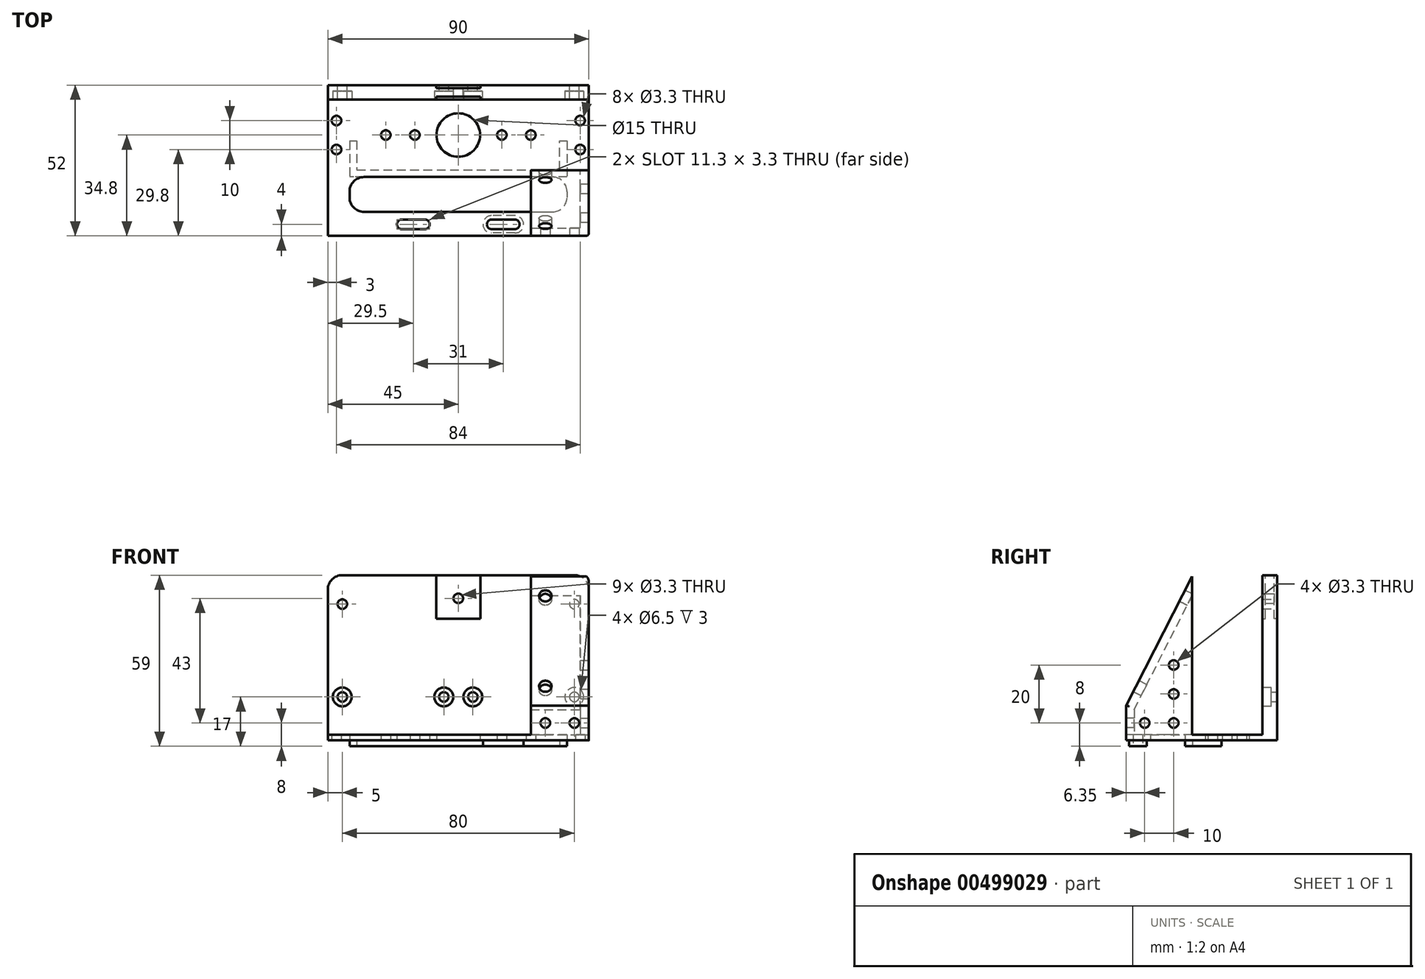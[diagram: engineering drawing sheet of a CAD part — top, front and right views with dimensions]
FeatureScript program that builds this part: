
annotation { "Feature Type Name" : "Feature", "Feature Type Description" : "" }
export const myFeature = defineFeature(function(context is Context, id is Id, definition is map)
    precondition{}
    {
        {
            var Q0;
            Q0=qCreatedBy(makeId("Top.planeOp"),FACE);
            var sketch = newSketch(context, id + "F0", { "sketchPlane" : qUnion([Q0])});
            skLineSegment(sketch, "E0.bottom", {"start": v(-45, 17.2) * mm, "end": v(45, 17.2) * mm});
            skLineSegment(sketch, "E0.top", {"start": v(-45, -34.8) * mm, "end": v(45, -34.8) * mm});
            skLineSegment(sketch, "E0.left", {"start": v(-45, 17.2) * mm, "end": v(-45, -34.8) * mm});
            skLineSegment(sketch, "E0.right", {"start": v(45, 17.2) * mm, "end": v(45, -34.8) * mm});
            skPoint(sketch, "E1", {"position": v(0, 17.2) * mm});
            skPoint(sketch, "E2", {"position": v(45, -8.8) * mm});
            skLineSegment(sketch, "E3.bottom", {"start": v(-35, 12) * mm, "end": v(35, 12) * mm, "construction": true});
            skLineSegment(sketch, "E3.top", {"start": v(-35, -12) * mm, "end": v(35, -12) * mm, "construction": true});
            skLineSegment(sketch, "E3.left", {"start": v(-35, 12) * mm, "end": v(-35, -12) * mm, "construction": true});
            skLineSegment(sketch, "E3.right", {"start": v(35, 12) * mm, "end": v(35, -12) * mm, "construction": true});
            skPoint(sketch, "E4", {"position": v(0, 12) * mm});
            skPoint(sketch, "E5", {"position": v(35, 0) * mm});
            skCircle(sketch, "E6", {"center": v(-15, 0) * mm, "radius": 1.65 * mm});
            skLineSegment(sketch, "E7", {"start": v(-35, -12) * mm, "end": v(35, -12) * mm});
            skLineSegment(sketch, "E8", {"start": v(35, -12) * mm, "end": v(35, -2) * mm});
            skLineSegment(sketch, "E9", {"start": v(35, -2) * mm, "end": v(37.5, -2) * mm});
            skLineSegment(sketch, "E10", {"start": v(37.5, -2) * mm, "end": v(37.5, -14.5) * mm});
            skLineSegment(sketch, "E11", {"start": v(37.5, -14.5) * mm, "end": v(-37.5, -14.5) * mm});
            skLineSegment(sketch, "E12", {"start": v(-37.5, -14.5) * mm, "end": v(-37.5, -2) * mm});
            skLineSegment(sketch, "E13", {"start": v(-37.5, -2) * mm, "end": v(-35, -2) * mm});
            skLineSegment(sketch, "E14", {"start": v(-35, -2) * mm, "end": v(-35, -12) * mm});
            skLineSegment(sketch, "E15", {"start": v(-35, -12) * mm, "end": v(-37.5, -12) * mm});
            skLineSegment(sketch, "E16", {"start": v(35, -12) * mm, "end": v(37.5, -12) * mm});
            skCircle(sketch, "E17", {"center": v(-19.5, -30.8) * mm, "radius": 1.65 * mm});
            skCircle(sketch, "E18", {"center": v(-11.5, -30.8) * mm, "radius": 1.65 * mm});
            skLineSegment(sketch, "E19.bottom", {"start": v(-19.5, -29.15) * mm, "end": v(-11.5, -29.15) * mm});
            skLineSegment(sketch, "E19.top", {"start": v(-19.5, -32.45) * mm, "end": v(-11.5, -32.45) * mm});
            skLineSegment(sketch, "E19.left", {"start": v(-19.5, -29.15) * mm, "end": v(-19.5, -32.45) * mm});
            skLineSegment(sketch, "E19.right", {"start": v(-11.5, -29.15) * mm, "end": v(-11.5, -32.45) * mm});
            skLineSegment(sketch, "E20", {"start": v(-19.5, -30.8) * mm, "end": v(-11.5, -30.8) * mm, "construction": true});
            skPoint(sketch, "E21", {"position": v(-15.5, -30.8) * mm});
            skCircle(sketch, "E22.MirrorC", {"center": v(19.5, -30.8) * mm, "radius": 1.65 * mm});
            skCircle(sketch, "E23.MirrorC", {"center": v(11.5, -30.8) * mm, "radius": 1.65 * mm});
            skLineSegment(sketch, "E24.MirrorCS", {"start": v(19.5, -29.15) * mm, "end": v(11.5, -29.15) * mm});
            skLineSegment(sketch, "E25.MirrorCS", {"start": v(19.5, -32.45) * mm, "end": v(11.5, -32.45) * mm});
            skPoint(sketch, "E26.MirrorP", {"position": v(15.5, -30.8) * mm});
            skLineSegment(sketch, "E27.bottom", {"start": v(-37.5, -14.5) * mm, "end": v(37.5, -14.5) * mm});
            skLineSegment(sketch, "E27.top", {"start": v(-37.5, -26.5) * mm, "end": v(37.5, -26.5) * mm});
            skLineSegment(sketch, "E27.left", {"start": v(-37.5, -14.5) * mm, "end": v(-37.5, -26.5) * mm});
            skLineSegment(sketch, "E27.right", {"start": v(37.5, -14.5) * mm, "end": v(37.5, -26.5) * mm});
            skCircle(sketch, "E28", {"center": v(-25, 0) * mm, "radius": 1.65 * mm});
            skCircle(sketch, "E29.MirrorC", {"center": v(15, 0) * mm, "radius": 1.65 * mm});
            skCircle(sketch, "E30.MirrorC", {"center": v(25, 0) * mm, "radius": 1.65 * mm});
            skCircle(sketch, "E31", {"center": v(0, 0) * mm, "radius": 7.5 * mm});
            skCircle(sketch, "E32", {"center": v(-42, 5) * mm, "radius": 1.65 * mm});
            skCircle(sketch, "E33", {"center": v(-42, -5) * mm, "radius": 1.65 * mm});
            skLineSegment(sketch, "E34", {"start": v(-42, 5) * mm, "end": v(-42, -5) * mm, "construction": true});
            skPoint(sketch, "E35", {"position": v(-42, 0) * mm});
            skCircle(sketch, "E36.MirrorC", {"center": v(42, 5) * mm, "radius": 1.65 * mm});
            skCircle(sketch, "E37.MirrorC", {"center": v(42, -5) * mm, "radius": 1.65 * mm});
            skSolve(sketch);
        }
        {
            var Q0;
            Q0=makeQuery(id+"F0.imprint","IMPRINT",FACE,{"disambiguationData":[TD([[makeQuery(id+"F0.imprint","IMPRINT",EDGE,{"derivedFrom":sQuery(id+"F0.wireOp",EDGE,"E0.bottom")}),-1.0]])]});
            var Q1;
            Q1=makeQuery(id+"F0.imprint","IMPRINT",FACE,{"disambiguationData":[TD([[makeQuery(id+"F0.imprint","IMPRINT",EDGE,{"derivedFrom":sQuery(id+"F0.wireOp",EDGE,"E7")}),-1.0]])]});
            var Q2;
            {var subQ0=sQuery(id+"F0.wireOp",EDGE,"E13");Q2=makeQuery(id+"F0.imprint","IMPRINT",FACE,{"disambiguationData":[TD([[makeQuery(id+"F0.imprint","IMPRINT",EDGE,{"derivedFrom":subQ0}),-1.0]])]});}
            var Q3;
            Q3=makeQuery(id+"F0.imprint","IMPRINT",FACE,{"disambiguationData":[TD([[makeQuery(id+"F0.imprint","IMPRINT",EDGE,{"derivedFrom":sQuery(id+"F0.wireOp",EDGE,"E8")}),-1.0]])]});
            extrude(context, id + "F1", {"entities" : qUnion([Q0, Q1, Q2, Q3]), "depth" : 4 * mm});
        }
        {
            var Q0;
            {var subQ0=sQuery(id+"F0.wireOp",EDGE,"E13");Q0=makeQuery(id+"F0.imprint","IMPRINT",FACE,{"disambiguationData":[TD([[makeQuery(id+"F0.imprint","IMPRINT",EDGE,{"derivedFrom":subQ0}),-1.0]])]});}
            var Q1;
            Q1=makeQuery(id+"F0.imprint","IMPRINT",FACE,{"disambiguationData":[TD([[makeQuery(id+"F0.imprint","IMPRINT",EDGE,{"derivedFrom":sQuery(id+"F0.wireOp",EDGE,"E8")}),-1.0]])]});
            extrude(context, id + "F2", {"entities" : qUnion([Q0, Q1]), "operationType" : NewBodyOperationType.ADD, "offsetDistance" : 25 * mm, "depth" : 3 * mm});
        }
        {
            var Q0;
            Q0=makeQuery(id+"F1.opExtrude","CAP_FACE",FACE,{"disambiguationData":[OSD([sQuery(id+"F0.wireOp",EDGE,"E0.bottom"),sQuery(id+"F0.wireOp",EDGE,"E0.top"),sQuery(id+"F0.wireOp",EDGE,"E0.left"),sQuery(id+"F0.wireOp",EDGE,"E0.right"),sQuery(id+"F0.wireOp",EDGE,"E6")])],"isStart":false});
            var sketch = newSketch(context, id + "F3", { "sketchPlane" : qUnion([Q0])});
            skLineSegment(sketch, "E38.bottom", {"start": v(-45, 17.2) * mm, "end": v(45, 17.2) * mm});
            skLineSegment(sketch, "E38.top", {"start": v(-45, 12.2) * mm, "end": v(45, 12.2) * mm});
            skLineSegment(sketch, "E38.left", {"start": v(-45, 17.2) * mm, "end": v(-45, 12.2) * mm});
            skLineSegment(sketch, "E38.right", {"start": v(45, 17.2) * mm, "end": v(45, 12.2) * mm});
            skSolve(sketch);
        }
        {
            var Q0;
            Q0=makeQuery(id+"F3.imprint","IMPRINT",FACE,{"disambiguationData":[TD([[makeQuery(id+"F3.imprint","IMPRINT",EDGE,{"derivedFrom":sQuery(id+"F3.wireOp",EDGE,"E38.bottom")}),-1.0]])]});
            extrude(context, id + "F4", {"entities" : qUnion([Q0]), "operationType" : NewBodyOperationType.ADD, "depth" : 55 * mm});
        }
        {
            var Q0;
            Q0=makeQuery(id+"F4.opExtrude","CAP_FACE",FACE,{"disambiguationData":[OSD([sQuery(id+"F3.wireOp",EDGE,"E38.bottom"),sQuery(id+"F3.wireOp",EDGE,"E38.top"),sQuery(id+"F3.wireOp",EDGE,"E38.left"),sQuery(id+"F3.wireOp",EDGE,"E38.right")])],"isStart":false});
            var sketch = newSketch(context, id + "F5", { "sketchPlane" : qUnion([Q0])});
            skLineSegment(sketch, "E39.bottom", {"start": v(-7.65, 17.2) * mm, "end": v(7.65, 17.2) * mm});
            skLineSegment(sketch, "E39.top", {"start": v(-7.65, 16.2) * mm, "end": v(7.65, 16.2) * mm});
            skLineSegment(sketch, "E39.left", {"start": v(-7.65, 17.2) * mm, "end": v(-7.65, 16.2) * mm});
            skLineSegment(sketch, "E39.right", {"start": v(7.65, 17.2) * mm, "end": v(7.65, 16.2) * mm});
            skLineSegment(sketch, "E40.bottom", {"start": v(-7.65, 12.2) * mm, "end": v(7.65, 12.2) * mm});
            skLineSegment(sketch, "E40.top", {"start": v(-7.65, 13.2) * mm, "end": v(7.65, 13.2) * mm});
            skLineSegment(sketch, "E40.left", {"start": v(-7.65, 12.2) * mm, "end": v(-7.65, 13.2) * mm});
            skLineSegment(sketch, "E40.right", {"start": v(7.65, 12.2) * mm, "end": v(7.65, 13.2) * mm});
            skPoint(sketch, "E41", {"position": v(0, 17.2) * mm});
            skSolve(sketch);
        }
        {
            var Q0;
            Q0=makeQuery(id+"F5.imprint","IMPRINT",FACE,{"disambiguationData":[TD([[makeQuery(id+"F5.imprint","IMPRINT",EDGE,{"derivedFrom":sQuery(id+"F5.wireOp",EDGE,"E39.bottom")}),-1.0]])]});
            var Q1;
            Q1=makeQuery(id+"F5.imprint","IMPRINT",FACE,{"disambiguationData":[TD([[makeQuery(id+"F5.imprint","IMPRINT",EDGE,{"derivedFrom":sQuery(id+"F5.wireOp",EDGE,"E40.bottom")}),1.0]])]});
            extrude(context, id + "F6", {"entities" : qUnion([Q0, Q1]), "operationType" : NewBodyOperationType.REMOVE, "oppositeDirection" : true, "depth" : 15 * mm});
        }
        {
            var Q0;
            Q0=makeQuery(id+"F6.boolean.opBoolean","COPY",FACE,{"derivedFrom":makeQuery(id+"F6.opExtrude","SWEPT_FACE",FACE,{"disambiguationData":[OSD([sQuery(id+"F5.wireOp",EDGE,"E39.top")])]})});
            var sketch = newSketch(context, id + "F7", { "sketchPlane" : qUnion([Q0])});
            skCircle(sketch, "E42", {"center": v(0, 51) * mm, "radius": 1.65 * mm});
            skSolve(sketch);
        }
        {
            var Q0;
            Q0=makeQuery(id+"F7.imprint","IMPRINT",FACE,{"disambiguationData":[TD([[makeQuery(id+"F7.imprint","IMPRINT",EDGE,{"derivedFrom":sQuery(id+"F7.wireOp",EDGE,"E42")}),1.0]])]});
            extrude(context, id + "F8", {"entities" : qUnion([Q0]), "operationType" : NewBodyOperationType.REMOVE, "endBound" : BoundingType.UP_TO_NEXT, "oppositeDirection" : true, "depth" : 25 * mm});
        }
        {
            var Q0;
            Q0=makeQuery(id+"F4.boolean.opBoolean","MERGE",FACE,{"derivedFrom":[makeQuery(id+"F1.opExtrude","SWEPT_FACE",FACE,{"disambiguationData":[OSD([sQuery(id+"F0.wireOp",EDGE,"E0.bottom")])]}),makeQuery(id+"F4.opExtrude","SWEPT_FACE",FACE,{"disambiguationData":[OSD([sQuery(id+"F3.wireOp",EDGE,"E38.bottom")])]})]});
            var sketch = newSketch(context, id + "F9", { "sketchPlane" : qUnion([Q0])});
            skLineSegment(sketch, "E43", {"start": v(-45, 17) * mm, "end": v(45, 17) * mm, "construction": true});
            skCircle(sketch, "E44", {"center": v(-40, 17) * mm, "radius": 1.65 * mm});
            skCircle(sketch, "E45", {"center": v(-5, 17) * mm, "radius": 1.65 * mm});
            skCircle(sketch, "E46.MirrorC", {"center": v(40, 17) * mm, "radius": 1.65 * mm});
            skCircle(sketch, "E47.MirrorC", {"center": v(5, 17) * mm, "radius": 1.65 * mm});
            skCircle(sketch, "E48", {"center": v(-40, 49) * mm, "radius": 1.65 * mm});
            skCircle(sketch, "E49.MirrorC", {"center": v(40, 49) * mm, "radius": 1.65 * mm});
            skSolve(sketch);
        }
        {
            var Q0;
            Q0 = qSketchRegion(id + "F9", true);
            extrude(context, id + "F10", {"entities" : qUnion([Q0]), "operationType" : NewBodyOperationType.REMOVE, "endBound" : BoundingType.UP_TO_NEXT, "oppositeDirection" : true, "depth" : 25 * mm});
        }
        {
            var Q0;
            Q0=makeQuery(id+"F4.opExtrude","SWEPT_FACE",FACE,{"disambiguationData":[OSD([sQuery(id+"F3.wireOp",EDGE,"E38.top")])]});
            var sketch = newSketch(context, id + "F11", { "sketchPlane" : qUnion([Q0])});
            skCircle(sketch, "E50", {"center": v(5, 17) * mm, "radius": 3.25 * mm});
            skCircle(sketch, "E51", {"center": v(40, 17) * mm, "radius": 3.25 * mm});
            skCircle(sketch, "E52.MirrorC", {"center": v(-5, 17) * mm, "radius": 3.25 * mm});
            skCircle(sketch, "E53.MirrorC", {"center": v(-40, 17) * mm, "radius": 3.25 * mm});
            skSolve(sketch);
        }
        {
            var Q0;
            Q0 = qSketchRegion(id + "F11", true);
            extrude(context, id + "F12", {"entities" : qUnion([Q0]), "operationType" : NewBodyOperationType.REMOVE, "oppositeDirection" : true, "depth" : 3 * mm});
        }
        {
            var Q0;
            Q0=makeQuery(id+"F0.imprint","IMPRINT",FACE,{"disambiguationData":[TD([[makeQuery(id+"F0.imprint","IMPRINT",EDGE,{"derivedFrom":sQuery(id+"F0.wireOp",EDGE,"E0.bottom")}),-1.0]])]});
            var sketch = newSketch(context, id + "F13", { "sketchPlane" : qUnion([Q0])});
            skPoint(sketch, "E54.0", {"position": v(-15.5, -30.8) * mm});
            skLineSegment(sketch, "E55.bottom", {"start": v(-19.5, -33.8) * mm, "end": v(-11.5, -33.8) * mm});
            skLineSegment(sketch, "E55.top", {"start": v(-19.5, -27.8) * mm, "end": v(-11.5, -27.8) * mm});
            skLineSegment(sketch, "E55.left", {"start": v(-22.5, -30.8) * mm, "end": v(-22.5, -30.8) * mm});
            skLineSegment(sketch, "E55.right", {"start": v(-8.5, -30.8) * mm, "end": v(-8.5, -30.8) * mm});
            skPoint(sketch, "E56", {"position": v(-15.5, -33.8) * mm});
            skPoint(sketch, "E57", {"position": v(-22.5, -30.8) * mm});
            skPoint(sketch, "E58.visualSharp", {"position": v(-22.5, -33.8) * mm});
            skArc(sketch, "E58.filletArc", {"start": v(-22.5, -30.8) * mm, "mid": v(-21.62, -32.92) * mm, "end": v(-19.5, -33.8) * mm});
            skPoint(sketch, "E59.visualSharp", {"position": v(-22.5, -27.8) * mm});
            skArc(sketch, "E59.filletArc", {"start": v(-19.5, -27.8) * mm, "mid": v(-21.62, -28.68) * mm, "end": v(-22.5, -30.8) * mm});
            skPoint(sketch, "E60.visualSharp", {"position": v(-8.5, -27.8) * mm});
            skArc(sketch, "E60.filletArc", {"start": v(-8.5, -30.8) * mm, "mid": v(-9.38, -28.68) * mm, "end": v(-11.5, -27.8) * mm});
            skPoint(sketch, "E61.visualSharp", {"position": v(-8.5, -33.8) * mm});
            skArc(sketch, "E61.filletArc", {"start": v(-11.5, -33.8) * mm, "mid": v(-9.38, -32.92) * mm, "end": v(-8.5, -30.8) * mm});
            skArc(sketch, "E62.MirrorCS", {"start": v(11.5, -33.8) * mm, "mid": v(9.38, -32.92) * mm, "end": v(8.5, -30.8) * mm});
            skLineSegment(sketch, "E63.MirrorCS", {"start": v(19.5, -33.8) * mm, "end": v(11.5, -33.8) * mm});
            skArc(sketch, "E64.MirrorCS", {"start": v(22.5, -30.8) * mm, "mid": v(21.62, -32.92) * mm, "end": v(19.5, -33.8) * mm});
            skArc(sketch, "E65.MirrorCS", {"start": v(19.5, -27.8) * mm, "mid": v(21.62, -28.68) * mm, "end": v(22.5, -30.8) * mm});
            skLineSegment(sketch, "E66.MirrorCS", {"start": v(19.5, -27.8) * mm, "end": v(11.5, -27.8) * mm});
            skArc(sketch, "E67.MirrorCS", {"start": v(8.5, -30.8) * mm, "mid": v(9.38, -28.68) * mm, "end": v(11.5, -27.8) * mm});
            skSolve(sketch);
        }
        {
            var Q0;
            Q0=makeQuery(id+"F13.imprint","IMPRINT",FACE,{"disambiguationData":[TD([[makeQuery(id+"F13.imprint","IMPRINT",EDGE,{"derivedFrom":sQuery(id+"F13.wireOp",EDGE,"E55.bottom")}),1.0]])]});
            var Q1;
            Q1=makeQuery(id+"F13.imprint","IMPRINT",FACE,{"disambiguationData":[TD([[makeQuery(id+"F13.imprint","IMPRINT",EDGE,{"derivedFrom":sQuery(id+"F13.wireOp",EDGE,"E62.MirrorCS")}),-1.0]])]});
            extrude(context, id + "F14", {"entities" : qUnion([Q0, Q1]), "operationType" : NewBodyOperationType.REMOVE, "depth" : 2 * mm});
        }
        {
            var Q0;
            Q0=makeQuery(id+"F4.boolean.opBoolean","MERGE",FACE,{"derivedFrom":[makeQuery(id+"F1.opExtrude","SWEPT_FACE",FACE,{"disambiguationData":[OSD([sQuery(id+"F0.wireOp",EDGE,"E0.right")])]}),makeQuery(id+"F4.opExtrude","SWEPT_FACE",FACE,{"disambiguationData":[OSD([sQuery(id+"F3.wireOp",EDGE,"E38.right")])]})]});
            var sketch = newSketch(context, id + "F15", { "sketchPlane" : qUnion([Q0])});
            skLineSegment(sketch, "E68", {"start": v(-34.8, 4) * mm, "end": v(-34.8, 14) * mm});
            skLineSegment(sketch, "E69", {"start": v(-34.8, 14) * mm, "end": v(-12.1, 58.55) * mm});
            skLineSegment(sketch, "E70", {"start": v(-12.1, 58.55) * mm, "end": v(-12.1, 4) * mm});
            skLineSegment(sketch, "E71", {"start": v(-12.1, 4) * mm, "end": v(-34.8, 4) * mm});
            skLineSegment(sketch, "E72", {"start": v(-34.8, 14) * mm, "end": v(-32.13, 12.64) * mm});
            skLineSegment(sketch, "E73", {"start": v(-32.13, 12.64) * mm, "end": v(-12.1, 51.94) * mm});
            skLineSegment(sketch, "E74", {"start": v(-12.1, 58.55) * mm, "end": v(-12.1, 51.94) * mm});
            skLineSegment(sketch, "E75", {"start": v(-32.13, 12.64) * mm, "end": v(-32.13, 4) * mm});
            skLineSegment(sketch, "E76", {"start": v(-32.13, 4) * mm, "end": v(-34.8, 4) * mm});
            skSolve(sketch);
        }
        {
            var Q0;
            Q0=makeQuery(id+"F15.imprint","IMPRINT",FACE,{"disambiguationData":[TD([[makeQuery(id+"F15.imprint","IMPRINT",EDGE,{"derivedFrom":sQuery(id+"F15.wireOp",EDGE,"E68")}),-1.0]])]});
            var Q1;
            {var subQ0=sQuery(id+"F15.wireOp",EDGE,"E72");Q1=makeQuery(id+"F15.imprint","IMPRINT",FACE,{"disambiguationData":[TD([[makeQuery(id+"F15.imprint","IMPRINT",EDGE,{"derivedFrom":subQ0}),1.0]])]});}
            var Q2;
            Q2=makeQuery(id+"F15.imprint","IMPRINT",FACE,{"disambiguationData":[TD([[makeQuery(id+"F15.imprint","IMPRINT",EDGE,{"derivedFrom":sQuery(id+"F15.wireOp",EDGE,"E74")}),-1.0]])]});
            var Q3;
            Q3=makeQuery(id+"F15.imprint","IMPRINT",FACE,{"disambiguationData":[TD([[makeQuery(id+"F15.imprint","IMPRINT",EDGE,{"derivedFrom":sQuery(id+"F15.wireOp",EDGE,"E73")}),1.0]])]});
            var Q4;
            Q4=makeQuery(id+"F15.imprint","IMPRINT",FACE,{"disambiguationData":[TD([[makeQuery(id+"F15.imprint","IMPRINT",EDGE,{"derivedFrom":sQuery(id+"F15.wireOp",EDGE,"E70")}),-1.0]])]});
            extrude(context, id + "F16", {"entities" : qUnion([Q0, Q1, Q2, Q3, Q4]), "operationType" : NewBodyOperationType.ADD, "oppositeDirection" : true, "depth" : 3 * mm});
        }
        {
            var Q0;
            Q0=makeQuery(id+"F15.imprint","IMPRINT",FACE,{"disambiguationData":[TD([[makeQuery(id+"F15.imprint","IMPRINT",EDGE,{"derivedFrom":sQuery(id+"F15.wireOp",EDGE,"E68")}),-1.0]])]});
            var Q1;
            Q1=makeQuery(id+"F15.imprint","IMPRINT",FACE,{"disambiguationData":[TD([[makeQuery(id+"F15.imprint","IMPRINT",EDGE,{"derivedFrom":sQuery(id+"F15.wireOp",EDGE,"E73")}),1.0]])]});
            var Q2;
            Q2=makeQuery(id+"F15.imprint","IMPRINT",FACE,{"disambiguationData":[TD([[makeQuery(id+"F15.imprint","IMPRINT",EDGE,{"derivedFrom":sQuery(id+"F15.wireOp",EDGE,"E74")}),-1.0]])]});
            extrude(context, id + "F17", {"entities" : qUnion([Q0, Q1, Q2]), "operationType" : NewBodyOperationType.ADD, "oppositeDirection" : true, "depth" : 20 * mm});
        }
        {
            var Q0;
            {var subQ0=sQuery(id+"F15.wireOp",EDGE,"1dctdDmi-W59R-1fRP-TE5Q-M4lD137gEtmT");var subQ1=sQuery(id+"F15.wireOp",EDGE,"E69");Q0=makeQuery(id+"F17.boolean.opBoolean","MERGE",FACE,{"derivedFrom":[makeQuery(id+"F16.opExtrude","SWEPT_FACE",FACE,{"disambiguationData":[OSD([subQ1,subQ0])]}),makeQuery(id+"F17.opExtrude","SWEPT_FACE",FACE,{"disambiguationData":[OSD([subQ1])]}),makeQuery(id+"F17.opExtrude","SWEPT_FACE",FACE,{"disambiguationData":[OSD([subQ0])]})]});}
            var sketch = newSketch(context, id + "F18", { "sketchPlane" : qUnion([Q0])});
            skCircle(sketch, "E77", {"center": v(30, 39.18) * mm, "radius": 2.15 * mm});
            skCircle(sketch, "E78", {"center": v(30, 4.18) * mm, "radius": 2.15 * mm});
            skLineSegment(sketch, "E79", {"start": v(30, 39.18) * mm, "end": v(30, 4.18) * mm, "construction": true});
            skPoint(sketch, "E80", {"position": v(30, 21.68) * mm});
            skPoint(sketch, "E81", {"position": v(45, 21.68) * mm});
            skSolve(sketch);
        }
        {
            var Q0;
            Q0=makeQuery(id+"F18.imprint","IMPRINT",FACE,{"disambiguationData":[TD([[makeQuery(id+"F18.imprint","IMPRINT",EDGE,{"derivedFrom":sQuery(id+"F18.wireOp",EDGE,"E78")}),1.0]])]});
            var Q1;
            Q1=makeQuery(id+"F18.imprint","IMPRINT",FACE,{"disambiguationData":[TD([[makeQuery(id+"F18.imprint","IMPRINT",EDGE,{"derivedFrom":sQuery(id+"F18.wireOp",EDGE,"E77")}),1.0]])]});
            extrude(context, id + "F19", {"entities" : qUnion([Q0, Q1]), "operationType" : NewBodyOperationType.REMOVE, "endBound" : BoundingType.UP_TO_NEXT, "oppositeDirection" : true, "depth" : 25 * mm});
        }
        {
            var Q0;
            {var subQ0=sQuery(id+"F15.wireOp",EDGE,"E68");Q0=makeQuery(id+"FYoWc9Rnscle1AE_1.1.F17.boolean.opBoolean","MERGE",FACE,{"derivedFrom":[makeQuery(id+"FYoWc9Rnscle1AE_1.1.F16.boolean.opBoolean","MERGE",FACE,{"derivedFrom":[makeQuery(id+"F17.boolean.opBoolean","MERGE",FACE,{"derivedFrom":[makeQuery(id+"F16.boolean.opBoolean","MERGE",FACE,{"derivedFrom":[makeQuery(id+"F1.opExtrude","SWEPT_FACE",FACE,{"disambiguationData":[OSD([sQuery(id+"F0.wireOp",EDGE,"E0.top")])]}),makeQuery(id+"F16.opExtrude","SWEPT_FACE",FACE,{"disambiguationData":[OSD([subQ0])]})]}),makeQuery(id+"F17.opExtrude","SWEPT_FACE",FACE,{"disambiguationData":[OSD([subQ0])]})]}),makeQuery(id+"FYoWc9Rnscle1AE_1.1.F16.opExtrude","SWEPT_FACE",FACE,{"disambiguationData":[OSD([subQ0])]})]}),makeQuery(id+"FYoWc9Rnscle1AE_1.1.F17.opExtrude","SWEPT_FACE",FACE,{"disambiguationData":[OSD([subQ0])]})]});}
            var sketch = newSketch(context, id + "F20", { "sketchPlane" : qUnion([Q0])});
            skCircle(sketch, "E82", {"center": v(40, 8) * mm, "radius": 1.65 * mm});
            skCircle(sketch, "E83", {"center": v(30, 8) * mm, "radius": 1.65 * mm});
            skLineSegment(sketch, "E84", {"start": v(30, 8) * mm, "end": v(40, 8) * mm, "construction": true});
            skPoint(sketch, "E85", {"position": v(35, 8) * mm});
            skPoint(sketch, "E86", {"position": v(35, 14) * mm});
            skSolve(sketch);
        }
        {
            var Q0;
            Q0 = qSketchRegion(id + "F20", true);
            extrude(context, id + "F21", {"entities" : qUnion([Q0]), "operationType" : NewBodyOperationType.REMOVE, "endBound" : BoundingType.UP_TO_NEXT, "oppositeDirection" : true, "depth" : 25 * mm});
        }
        {
            var Q0;
            Q0=makeQuery(id+"F16.boolean.opBoolean","MERGE",FACE,{"derivedFrom":[makeQuery(id+"F4.boolean.opBoolean","MERGE",FACE,{"derivedFrom":[makeQuery(id+"F1.opExtrude","SWEPT_FACE",FACE,{"disambiguationData":[OSD([sQuery(id+"F0.wireOp",EDGE,"E0.right")])]}),makeQuery(id+"F4.opExtrude","SWEPT_FACE",FACE,{"disambiguationData":[OSD([sQuery(id+"F3.wireOp",EDGE,"E38.right")])]})]}),makeQuery(id+"F16.opExtrude","CAP_FACE",FACE,{"disambiguationData":[OSD([sQuery(id+"F15.wireOp",EDGE,"E68"),sQuery(id+"F15.wireOp",EDGE,"E69"),sQuery(id+"F15.wireOp",EDGE,"E70"),sQuery(id+"F15.wireOp",EDGE,"E71"),sQuery(id+"F15.wireOp",EDGE,"E74"),sQuery(id+"F15.wireOp",EDGE,"1dctdDmi-W59R-1fRP-TE5Q-M4lD137gEtmT"),sQuery(id+"F15.wireOp",EDGE,"E76")])],"isStart":true})]});
            var sketch = newSketch(context, id + "F22", { "sketchPlane" : qUnion([Q0])});
            skCircle(sketch, "E87", {"center": v(-28.45, 8) * mm, "radius": 1.65 * mm});
            skCircle(sketch, "E88", {"center": v(-18.45, 8) * mm, "radius": 1.65 * mm});
            skLineSegment(sketch, "E89", {"start": v(-28.45, 8) * mm, "end": v(-18.45, 8) * mm, "construction": true});
            skPoint(sketch, "E90", {"position": v(-23.45, 8) * mm});
            skLineSegment(sketch, "E91", {"start": v(-18.45, 8) * mm, "end": v(-12.1, 8) * mm, "construction": true});
            skLineSegment(sketch, "E92", {"start": v(-28.45, 8) * mm, "end": v(-34.8, 8) * mm, "construction": true});
            skCircle(sketch, "E93", {"center": v(-18.45, 18) * mm, "radius": 1.65 * mm});
            skCircle(sketch, "E94", {"center": v(-18.45, 28) * mm, "radius": 1.65 * mm});
            skSolve(sketch);
        }
        {
            var Q0;
            Q0 = qSketchRegion(id + "F22", true);
            extrude(context, id + "F23", {"entities" : qUnion([Q0]), "operationType" : NewBodyOperationType.REMOVE, "endBound" : BoundingType.UP_TO_NEXT, "oppositeDirection" : true, "depth" : 25 * mm});
        }
        {
            var Q0;
            {var subQ0=sQuery(id+"F15.wireOp",EDGE,"1dctdDmi-W59R-1fRP-TE5Q-M4lD137gEtmT");var subQ1=sQuery(id+"F15.wireOp",EDGE,"E74");Q0=makeQuery(id+"F17.boolean.opBoolean","MERGE",EDGE,{"derivedFrom":[makeQuery(id+"F16.opExtrude","SWEPT_EDGE",EDGE,{"disambiguationData":[OSD([subQ1,subQ0])]}),makeQuery(id+"F17.opExtrude","SWEPT_EDGE",EDGE,{"disambiguationData":[OSD([subQ1,subQ0])]})]});}
            var Q1;
            Q1=makeQuery(id+"F16.boolean.opBoolean","MERGE",EDGE,{"derivedFrom":[makeQuery(id+"F1.opExtrude","SWEPT_EDGE",EDGE,{"disambiguationData":[OSD([sQuery(id+"F0.wireOp",EDGE,"E0.top"),sQuery(id+"F0.wireOp",EDGE,"E0.right")])]}),makeQuery(id+"F16.opExtrude","CAP_EDGE",EDGE,{"disambiguationData":[OSD([sQuery(id+"F15.wireOp",EDGE,"E68")])],"isStart":true})]});
            var Q2;
            Q2=makeQuery(id+"F16.opExtrude","CAP_EDGE",EDGE,{"disambiguationData":[OSD([sQuery(id+"F15.wireOp",EDGE,"E69"),sQuery(id+"F15.wireOp",EDGE,"1dctdDmi-W59R-1fRP-TE5Q-M4lD137gEtmT")])],"isStart":true});
            fillet(context, id + "F24", {"entities" : qUnion([Q0, Q1, Q2]), "radius" : 1 * mm, "tangentPropagation" : true, "allowEdgeOverflow" : false});
        }
        {
            var Q0;
            Q0=makeQuery(id+"F4.opExtrude","CAP_EDGE",EDGE,{"disambiguationData":[OSD([sQuery(id+"F3.wireOp",EDGE,"E38.right")])],"isStart":false});
            var Q1;
            Q1=makeQuery(id+"F4.opExtrude","CAP_EDGE",EDGE,{"disambiguationData":[OSD([sQuery(id+"F3.wireOp",EDGE,"E38.left")])],"isStart":false});
            var Q2;
            Q2=makeQuery(id+"FHVHkK3Abyfqzx4_1.opExtrude","CAP_EDGE",EDGE,{"disambiguationData":[OSD([sQuery(id+"F0.wireOp",EDGE,"E10")])],"isStart":false});
            var Q3;
            Q3=makeQuery(id+"FHVHkK3Abyfqzx4_1.opExtrude","CAP_EDGE",EDGE,{"disambiguationData":[OSD([sQuery(id+"F0.wireOp",EDGE,"E12")])],"isStart":false});
            var Q4;
            Q4=makeQuery(id+"F1.opExtrude","SWEPT_EDGE",EDGE,{"disambiguationData":[OSD([sQuery(id+"F0.wireOp",EDGE,"E27.top"),sQuery(id+"F0.wireOp",EDGE,"E27.right")])]});
            var Q5;
            Q5=makeQuery(id+"F1.opExtrude","SWEPT_EDGE",EDGE,{"disambiguationData":[OSD([sQuery(id+"F0.wireOp",EDGE,"E10"),sQuery(id+"F0.wireOp",EDGE,"E27.bottom"),sQuery(id+"F0.wireOp",EDGE,"E27.right")])]});
            var Q6;
            Q6=makeQuery(id+"F1.opExtrude","SWEPT_EDGE",EDGE,{"disambiguationData":[OSD([sQuery(id+"F0.wireOp",EDGE,"E12"),sQuery(id+"F0.wireOp",EDGE,"E27.bottom"),sQuery(id+"F0.wireOp",EDGE,"E27.left")])]});
            var Q7;
            Q7=makeQuery(id+"F1.opExtrude","SWEPT_EDGE",EDGE,{"disambiguationData":[OSD([sQuery(id+"F0.wireOp",EDGE,"E27.top"),sQuery(id+"F0.wireOp",EDGE,"E27.left")])]});
            fillet(context, id + "F25", {"entities" : qUnion([Q0, Q1, Q2, Q3, Q4, Q5, Q6, Q7]), "radius" : 5 * mm, "tangentPropagation" : true, "allowEdgeOverflow" : false});
        }
    });
